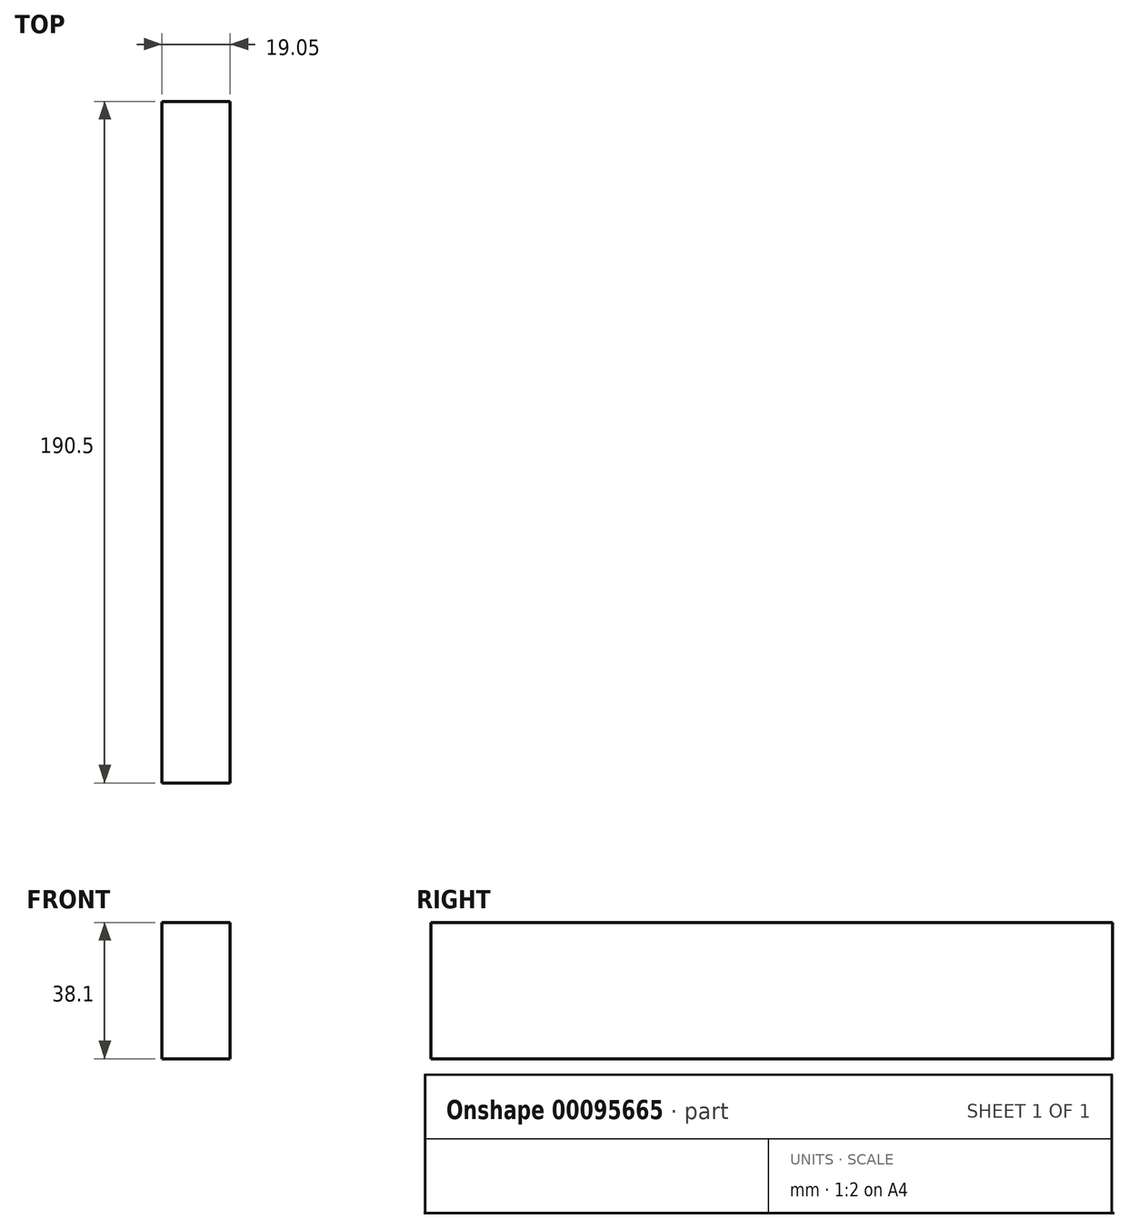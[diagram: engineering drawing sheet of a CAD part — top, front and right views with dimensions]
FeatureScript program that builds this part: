
annotation { "Feature Type Name" : "Feature", "Feature Type Description" : "" }
export const myFeature = defineFeature(function(context is Context, id is Id, definition is map)
    precondition{}
    {
        {
            var Q0;
            Q0=qCreatedBy(makeId("Right.planeOp"),FACE);
            var sketch = newSketch(context, id + "F0", { "sketchPlane" : qUnion([Q0])});
            skLineSegment(sketch, "E0.bottom", {"start": v(-436.58, -32.2) * mm, "end": v(-246.08, -32.2) * mm});
            skLineSegment(sketch, "E0.top", {"start": v(-436.58, -70.3) * mm, "end": v(-246.08, -70.3) * mm});
            skLineSegment(sketch, "E0.left", {"start": v(-436.58, -32.2) * mm, "end": v(-436.58, -70.3) * mm});
            skLineSegment(sketch, "E0.right", {"start": v(-246.08, -32.2) * mm, "end": v(-246.08, -70.3) * mm});
            skSolve(sketch);
        }
        {
            var Q0;
            Q0=makeQuery(id+"F0.imprint","IMPRINT",FACE,{"disambiguationData":[TD([[makeQuery(id+"F0.imprint","IMPRINT",EDGE,{"derivedFrom":sQuery(id+"F0.wireOp",EDGE,"E0.bottom")}),-1.0]])]});
            extrude(context, id + "F1", {"entities" : qUnion([Q0]), "depth" : 19.05 * mm});
        }
    });
